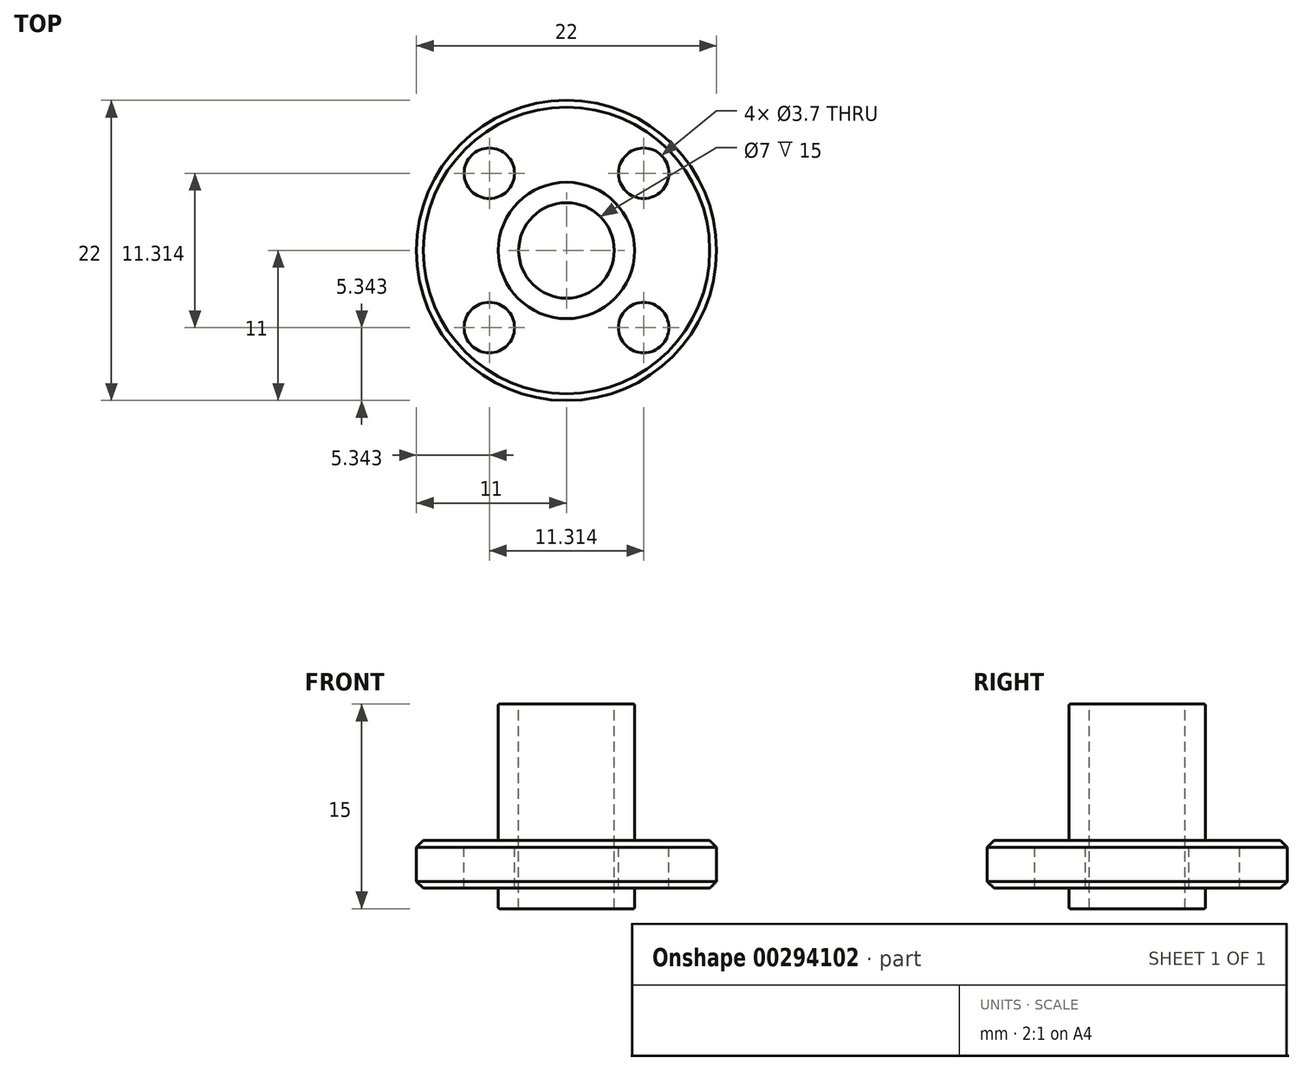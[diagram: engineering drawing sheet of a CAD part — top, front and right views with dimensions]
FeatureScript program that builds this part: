
annotation { "Feature Type Name" : "Feature", "Feature Type Description" : "" }
export const myFeature = defineFeature(function(context is Context, id is Id, definition is map)
    precondition{}
    {
        {
            var Q0;
            Q0=qCreatedBy(makeId("Top.planeOp"),FACE);
            var sketch = newSketch(context, id + "F0", { "sketchPlane" : qUnion([Q0])});
            skCircle(sketch, "E0", {"center": v(0, 0) * mm, "radius": 5 * mm});
            skCircle(sketch, "E1", {"center": v(0, 0) * mm, "radius": 11 * mm});
            skLineSegment(sketch, "E2", {"start": v(-7.78, 7.78) * mm, "end": v(7.78, -7.78) * mm, "construction": true});
            skLineSegment(sketch, "E3", {"start": v(-7.78, -7.78) * mm, "end": v(7.78, 7.78) * mm, "construction": true});
            skCircle(sketch, "E4", {"center": v(-5.66, 5.66) * mm, "radius": 1.85 * mm});
            skCircle(sketch, "E5", {"center": v(5.66, 5.66) * mm, "radius": 1.85 * mm});
            skCircle(sketch, "E6", {"center": v(5.66, -5.66) * mm, "radius": 1.85 * mm});
            skCircle(sketch, "E7", {"center": v(-5.66, -5.66) * mm, "radius": 1.85 * mm});
            skCircle(sketch, "E8", {"center": v(0, 0) * mm, "radius": 3.5 * mm});
            skCircle(sketch, "E9", {"center": v(0, 0) * mm, "radius": 8 * mm, "construction": true});
            skSolve(sketch);
        }
        {
            var Q0;
            Q0=makeQuery(id+"F0.imprint","IMPRINT",FACE,{"disambiguationData":[TD([[makeQuery(id+"F0.imprint","IMPRINT",EDGE,{"derivedFrom":sQuery(id+"F0.wireOp",EDGE,"E0")}),-1.0]])]});
            var Q1;
            Q1=makeQuery(id+"F0.imprint","IMPRINT",FACE,{"disambiguationData":[TD([[makeQuery(id+"F0.imprint","IMPRINT",EDGE,{"derivedFrom":sQuery(id+"F0.wireOp",EDGE,"E0")}),1.0]])]});
            extrude(context, id + "F1", {"entities" : qUnion([Q0, Q1]), "oppositeDirection" : true, "depth" : 3.5 * mm, "flatOperationType" : FlatOperationType.REMOVE, "offsetDistance" : 25 * mm, "domain" : OperationDomain.MODEL});
        }
        {
            var Q0;
            Q0=makeQuery(id+"F0.imprint","IMPRINT",FACE,{"disambiguationData":[TD([[makeQuery(id+"F0.imprint","IMPRINT",EDGE,{"derivedFrom":sQuery(id+"F0.wireOp",EDGE,"E0")}),1.0]])]});
            extrude(context, id + "F2", {"entities" : qUnion([Q0]), "operationType" : NewBodyOperationType.ADD, "depth" : 10 * mm, "hasSecondDirection" : true, "secondDirectionOppositeDirection" : true, "secondDirectionDepth" : 5 * mm, "flatOperationType" : FlatOperationType.REMOVE, "offsetDistance" : 25 * mm, "domain" : OperationDomain.MODEL});
        }
        {
            var Q0;
            Q0=makeQuery(id+"F1.opExtrude","CAP_EDGE",EDGE,{"disambiguationData":[OSD([sQuery(id+"F0.wireOp",EDGE,"E1")])],"isStart":true});
            var Q1;
            Q1=makeQuery(id+"F1.opExtrude","CAP_EDGE",EDGE,{"disambiguationData":[OSD([sQuery(id+"F0.wireOp",EDGE,"E1")])],"isStart":false});
            chamfer(context, id + "F3", {"entities" : qUnion([Q0, Q1]), "width" : 0.5 * mm, "tangentPropagation" : true});
        }
        {
            var Q0;
            Q0=makeQuery(id+"F2.opExtrude","CAP_EDGE",EDGE,{"disambiguationData":[OSD([sQuery(id+"F0.wireOp",EDGE,"E0")])],"isStart":false});
            var Q1;
            Q1=makeQuery(id+"F2.boolean.opBoolean","INTERSECT",EDGE,{"derivedFrom":[makeQuery(id+"F1.opExtrude","CAP_FACE",FACE,{"disambiguationData":[OSD([sQuery(id+"F0.wireOp",EDGE,"E1"),sQuery(id+"F0.wireOp",EDGE,"E4"),sQuery(id+"F0.wireOp",EDGE,"E5"),sQuery(id+"F0.wireOp",EDGE,"E6"),sQuery(id+"F0.wireOp",EDGE,"E7"),sQuery(id+"F0.wireOp",EDGE,"E8")])],"isStart":true}),makeQuery(id+"F2.opExtrude","SWEPT_FACE",FACE,{"disambiguationData":[OSD([sQuery(id+"F0.wireOp",EDGE,"E0")])]})]});
            var Q2;
            Q2=makeQuery(id+"F2.boolean.opBoolean","INTERSECT",EDGE,{"derivedFrom":[makeQuery(id+"F1.opExtrude","CAP_FACE",FACE,{"disambiguationData":[OSD([sQuery(id+"F0.wireOp",EDGE,"E1"),sQuery(id+"F0.wireOp",EDGE,"E4"),sQuery(id+"F0.wireOp",EDGE,"E5"),sQuery(id+"F0.wireOp",EDGE,"E6"),sQuery(id+"F0.wireOp",EDGE,"E7"),sQuery(id+"F0.wireOp",EDGE,"E8")])],"isStart":false}),makeQuery(id+"F2.opExtrude","SWEPT_FACE",FACE,{"disambiguationData":[OSD([sQuery(id+"F0.wireOp",EDGE,"E0")])]})]});
            var Q3;
            Q3=makeQuery(id+"F2.opExtrude","CAP_EDGE",EDGE,{"disambiguationData":[OSD([sQuery(id+"F0.wireOp",EDGE,"E0")])],"isStart":true});
            fillet(context, id + "F4", {"entities" : qUnion([Q0, Q1, Q2, Q3]), "radius" : 0.1 * mm, "tangentPropagation" : true, "allowEdgeOverflow" : false});
        }
    });
